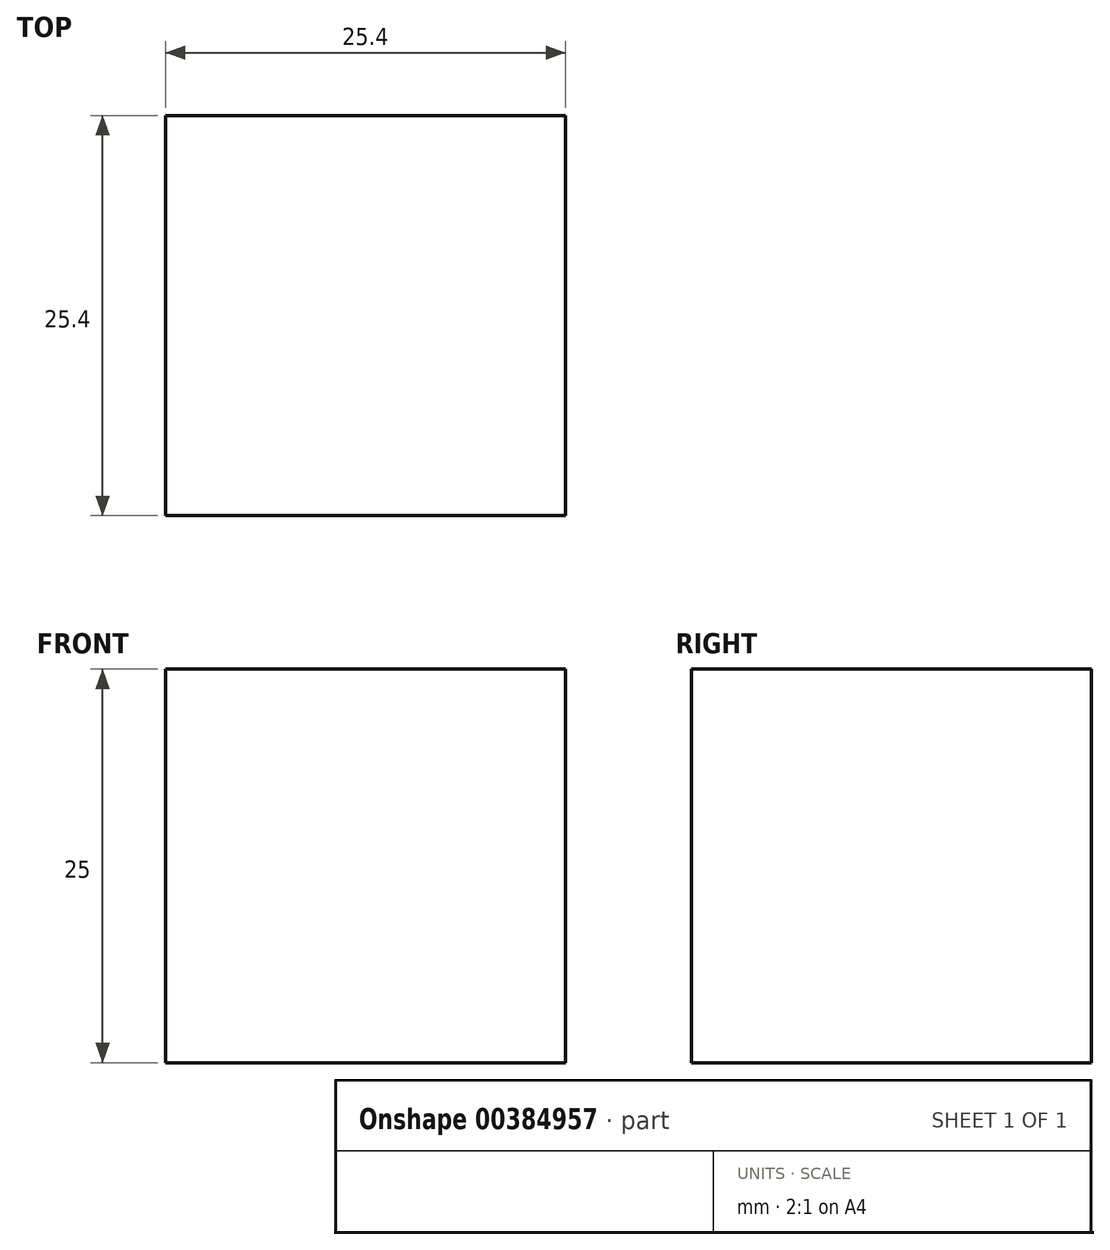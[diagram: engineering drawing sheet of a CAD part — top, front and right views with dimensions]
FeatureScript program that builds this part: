
annotation { "Feature Type Name" : "Feature", "Feature Type Description" : "" }
export const myFeature = defineFeature(function(context is Context, id is Id, definition is map)
    precondition{}
    {
        {
            var Q0;
            Q0=qCreatedBy(makeId("Top.planeOp"),FACE);
            var sketch = newSketch(context, id + "F0", { "sketchPlane" : qUnion([Q0])});
            skLineSegment(sketch, "E0.bottom", {"start": v(0, 0) * mm, "end": v(25.4, 0) * mm});
            skLineSegment(sketch, "E0.top", {"start": v(0, -25.4) * mm, "end": v(25.4, -25.4) * mm});
            skLineSegment(sketch, "E0.left", {"start": v(0, 0) * mm, "end": v(0, -25.4) * mm});
            skLineSegment(sketch, "E0.right", {"start": v(25.4, 0) * mm, "end": v(25.4, -25.4) * mm});
            skSolve(sketch);
        }
        {
            var Q0;
            Q0 = qSketchRegion(id + "F0", true);
            extrude(context, id + "F1", {"entities" : qUnion([Q0]), "depth" : 25 * mm});
        }
    });
